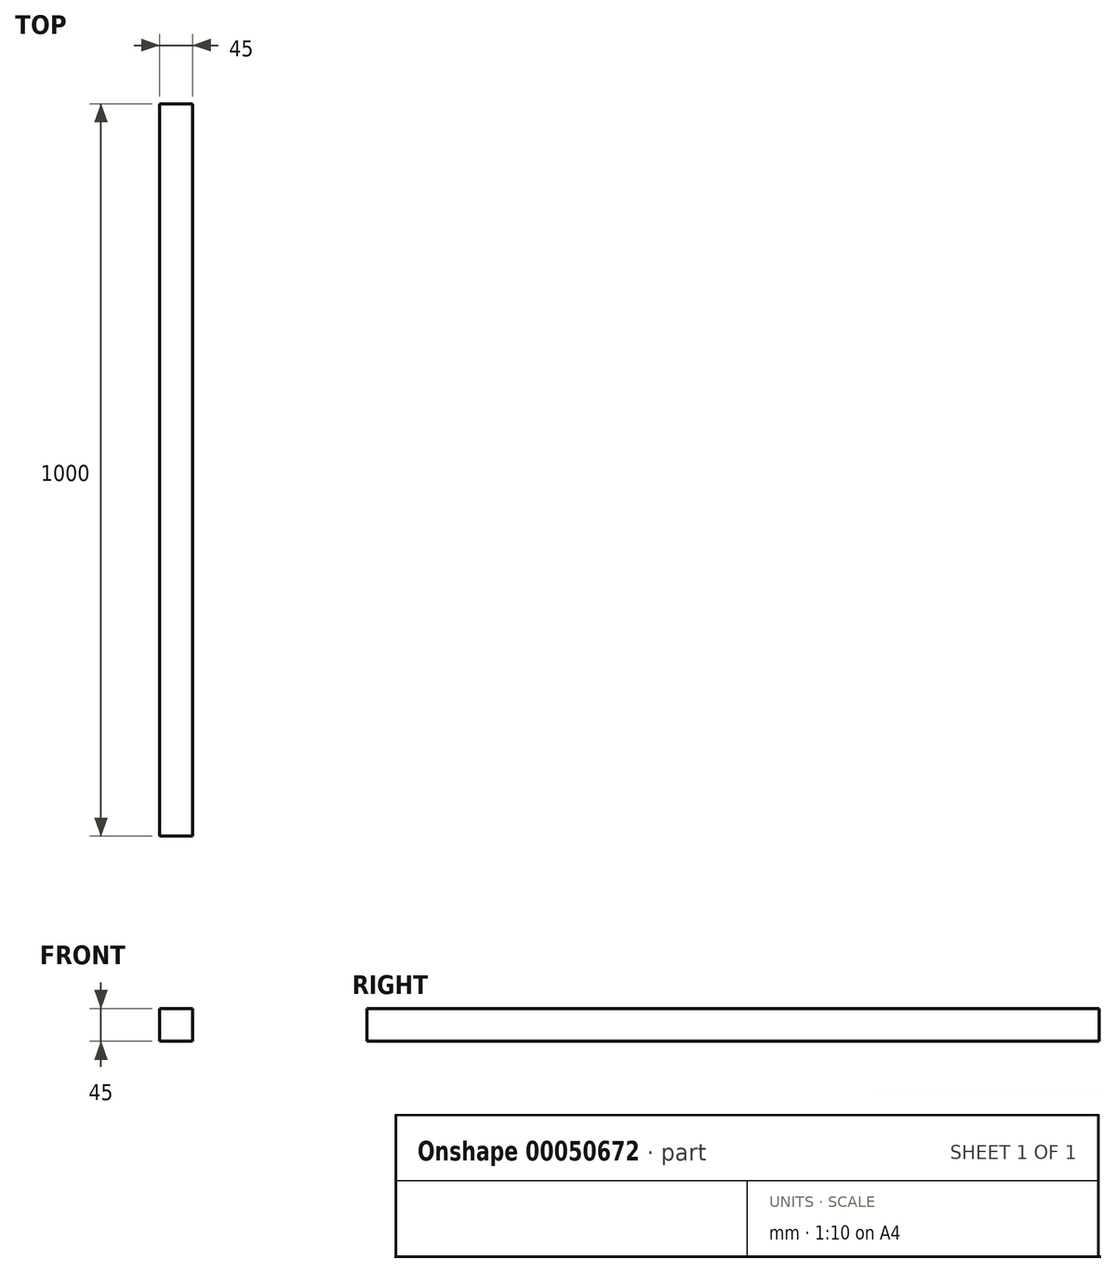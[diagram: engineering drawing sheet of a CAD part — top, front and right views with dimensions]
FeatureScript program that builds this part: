
annotation { "Feature Type Name" : "Feature", "Feature Type Description" : "" }
export const myFeature = defineFeature(function(context is Context, id is Id, definition is map)
    precondition{}
    {
        {
            assignVariable(context, id + "F0", {"name" : "L", "anyValue" : 1000});
        }
        {
            var Q0;
            Q0=qCreatedBy(makeId("Front.planeOp"),FACE);
            var sketch = newSketch(context, id + "F1", { "sketchPlane" : qUnion([Q0])});
            skLineSegment(sketch, "E0.bottom", {"start": v(0, 2.99) * mm, "end": v(45, 2.99) * mm});
            skLineSegment(sketch, "E0.top", {"start": v(0, 47.99) * mm, "end": v(45, 47.99) * mm});
            skLineSegment(sketch, "E0.left", {"start": v(0, 2.99) * mm, "end": v(0, 47.99) * mm});
            skLineSegment(sketch, "E0.right", {"start": v(45, 2.99) * mm, "end": v(45, 47.99) * mm});
            skSolve(sketch);
        }
        {
            var Q0;
            Q0=makeQuery(id+"F1.imprint","IMPRINT",FACE,{"disambiguationData":[TD([[makeQuery(id+"F1.imprint","IMPRINT",EDGE,{"derivedFrom":sQuery(id+"F1.wireOp",EDGE,"E0.bottom")}),1.0]])]});
            extrude(context, id + "F2", {"entities" : qUnion([Q0]), "depth" : (getVariable(context, 'L')) * mm, "offsetDistance" : 25 * mm});
        }
    });
